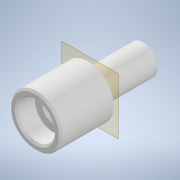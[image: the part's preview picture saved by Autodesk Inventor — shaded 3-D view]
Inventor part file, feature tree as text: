
AUTODESK INVENTOR PART (.ipt)
format: ipt  version: 2021 (Build 250183000, 183)  size: 150,016 bytes
history: native  units: mm
features: other x4, extrude x4, sketch x4, reference x3, chamfer x1, projected_geometry x1
ambient origin geometry x8: Origin, YZ Plane, XZ Plane, XY Plane, X Axis, Y Axis, Z Axis, Center Point
bodies: Body1 (feature_tree)
feature tree (17):
  other  "Bryła1"
  other  "Płaszczyzna konstrukcyjna1"
  extrude  "Wyciągnięcie proste1"  Depth=4.0mm
  extrude  "Wyciągnięcie proste2"  Depth=30.0mm TaperAngle=0.0deg
  extrude  "Wyciągnięcie proste3"  Depth=30.0mm TaperAngle=0.0deg
  extrude  "Wyciągnięcie proste4"  Depth=20.0mm
  chamfer  "Faza1"  Distance=10.0mm
  sketch  "Szkic1"
  reference  "Odniesienie1"
  reference  "Odniesienie2"
  sketch  "Szkic2"
  projected_geometry  "Pętla rzutowana1"
  reference  "Odniesienie3"
  sketch  "Szkic3"
  sketch  "Szkic4"
  other  "wszystko.iam"
  other  "fiolka:1"
